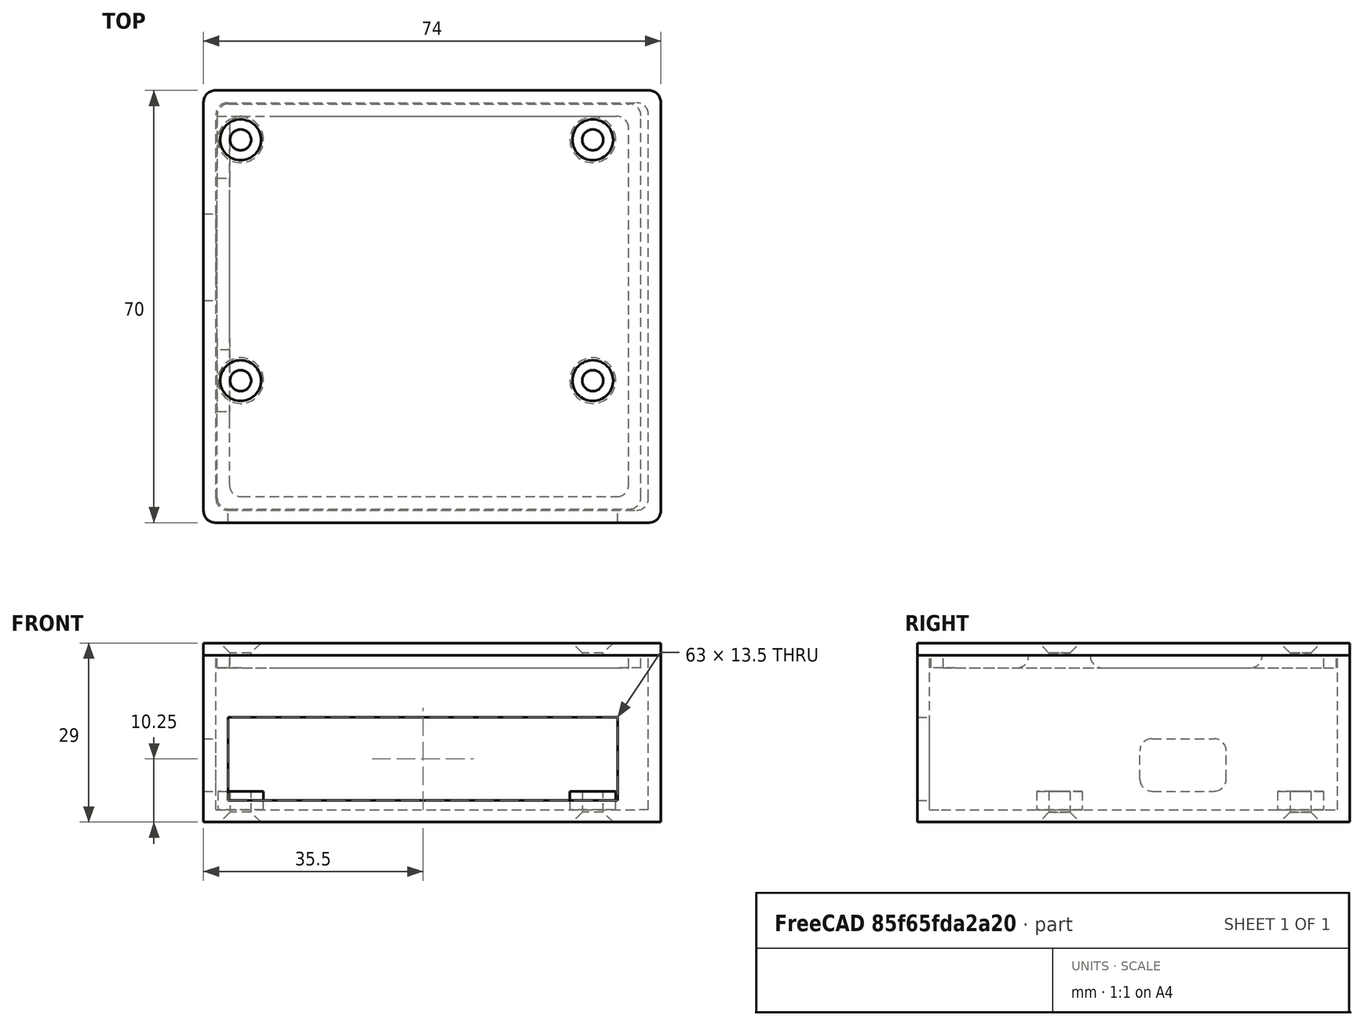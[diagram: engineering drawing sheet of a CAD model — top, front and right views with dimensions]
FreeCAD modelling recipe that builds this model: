
FCSTD DOCUMENT  (FreeCAD 0.20R29410 (Git))
Label: USB_RS232_Adapter_V1
License: All rights reserved
LicenseURL: http://en.wikipedia.org/wiki/All_rights_reserved
objects: Part::Cut×14, Part::Box×9, Part::Cylinder×8, Part::Fillet×6, Part::Fuse×5, Part::Chamfer×2
note: 44 computed .brp shape members not serialized (recipe doc carries the construction recipe); baked Part::Feature solids carry a one-line shape summary decoded from their .brp

FEATURE [Part::Box] Box  label="Würfel"
  AttacherType = Attacher::AttachEngine3D
  Height = 25
  Length = 70
  Placement = pos=(0,-18,0) rot=(0,0,1;0rad)
  Width = 66
FEATURE [Part::Box] Box001  label="Würfel001"
  AttacherType = Attacher::AttachEngine3D
  Height = 27
  Length = 74
  Placement = pos=(-2,-20,-2) rot=(0,0,1;0rad)
  Width = 70
FEATURE [Part::Cut] Cut
  Base = -> Box001
  Tool = -> Box
FEATURE [Part::Cylinder] Cylinder  label="Zylinder"
  Angle = 360
  AttacherType = Attacher::AttachEngine3D
  FirstAngle = 0
  Height = 35
  Placement = pos=(4,3,-2) rot=(0,0,1;0rad)
  Radius = 1.7
  SecondAngle = 0
FEATURE [Part::Cylinder] Cylinder001  label="Zylinder001"
  Angle = 360
  AttacherType = Attacher::AttachEngine3D
  FirstAngle = 0
  Height = 35
  Placement = pos=(61,3,-2) rot=(0,0,1;0rad)
  Radius = 1.7
  SecondAngle = 0
FEATURE [Part::Cylinder] Cylinder002  label="Zylinder002"
  Angle = 360
  AttacherType = Attacher::AttachEngine3D
  FirstAngle = 0
  Height = 33
  Placement = pos=(61,42,-2) rot=(0,0,1;0rad)
  Radius = 1.7
  SecondAngle = 0
FEATURE [Part::Cylinder] Cylinder003  label="Zylinder003"
  Angle = 360
  AttacherType = Attacher::AttachEngine3D
  FirstAngle = 0
  Height = 35
  Placement = pos=(4,42,-2) rot=(0,0,1;0rad)
  Radius = 1.7
  SecondAngle = 0
FEATURE [Part::Box] Box002  label="Würfel002"
  AttacherType = Attacher::AttachEngine3D
  Height = 8.5
  Length = 15
  Placement = pos=(-2,16,3) rot=(0,0,1;0rad)
  Width = 14
FEATURE [Part::Cylinder] Cylinder004  label="Zylinder004"
  Angle = 360
  AttacherType = Attacher::AttachEngine3D
  FirstAngle = 0
  Height = 3
  Placement = pos=(4,3,0) rot=(0,0,1;0rad)
  Radius = 3.7
  SecondAngle = 0
FEATURE [Part::Cylinder] Cylinder005  label="Zylinder005"
  Angle = 360
  AttacherType = Attacher::AttachEngine3D
  FirstAngle = 0
  Height = 3
  Placement = pos=(61,42,0) rot=(0,0,1;0rad)
  Radius = 3.7
  SecondAngle = 0
FEATURE [Part::Cylinder] Cylinder006  label="Zylinder006"
  Angle = 360
  AttacherType = Attacher::AttachEngine3D
  FirstAngle = 0
  Height = 3
  Placement = pos=(61,3,0) rot=(0,0,1;0rad)
  Radius = 3.7
  SecondAngle = 0
FEATURE [Part::Cylinder] Cylinder007  label="Zylinder007"
  Angle = 360
  AttacherType = Attacher::AttachEngine3D
  FirstAngle = 0
  Height = 3
  Placement = pos=(4,42,0) rot=(0,0,1;0rad)
  Radius = 3.7
  SecondAngle = 0
FEATURE [Part::Box] Box003  label="Würfel003"
  AttacherType = Attacher::AttachEngine3D
  Height = 13.5
  Length = 63
  Placement = pos=(2,-28,1.5) rot=(0,0,1;0rad)
  Width = 10
FEATURE [Part::Fuse] Fusion
  Base = -> Cut
  Tool = -> Cylinder004
FEATURE [Part::Fuse] Fusion001
  Base = -> Fusion
  Tool = -> Cylinder005
FEATURE [Part::Fuse] Fusion002
  Base = -> Fusion001
  Tool = -> Cylinder006
FEATURE [Part::Fuse] Fusion003
  Base = -> Fusion002
  Tool = -> Cylinder007
FEATURE [Part::Cut] Cut001
  Base = -> Fusion003
  Tool = -> Cylinder
FEATURE [Part::Cut] Cut002
  Base = -> Cut001
  Tool = -> Cylinder001
FEATURE [Part::Cut] Cut003
  Base = -> Cut002
  Tool = -> Cylinder002
FEATURE [Part::Cut] Cut004
  Base = -> Cut003
  Tool = -> Cylinder003
FEATURE [Part::Cut] Cut005
  Base = -> Cut004
  Tool = -> Box002
FEATURE [Part::Cut] Cut006
  Base = -> Cut005
  Tool = -> Box003
FEATURE [Part::Fillet] Fillet
  Base = -> Cut006
  Edges = 4 edges r=2: [Edge29,Edge31,Edge32,Edge35]
FEATURE [Part::Fillet] Fillet001
  Base = -> Fillet
  Edges = 8 edges r=1.9: [Edge9,Edge11,Edge30,Edge48,Edge49,Edge51,Edge61,Edge62]
FEATURE [Part::Box] Box004  label="Würfel004"
  AttacherType = Attacher::AttachEngine3D
  Height = 2
  Length = 74
  Placement = pos=(-2,-20,25) rot=(0,0,1;0rad)
  Width = 70
FEATURE [Part::Box] Box005  label="Würfel005"
  AttacherType = Attacher::AttachEngine3D
  Height = 2
  Length = 68.6
  Placement = pos=(0.2,-17.8,23) rot=(0,0,1;0rad)
  Width = 65.6
FEATURE [Part::Fillet] Fillet002
  Base = -> Box004
  Edges = 4 edges r=1.9: [Edge1,Edge3,Edge5,Edge7]
FEATURE [Part::Fillet] Fillet003
  Base = -> Box005
  Edges = 4 edges r=1.9: [Edge1,Edge3,Edge5,Edge7]
FEATURE [Part::Box] Box006  label="Würfel006"
  AttacherType = Attacher::AttachEngine3D
  Height = 2
  Length = 64.6
  Placement = pos=(2.2,-15.8,23) rot=(0,0,1;0rad)
  Width = 61.6
FEATURE [Part::Fillet] Fillet004
  Base = -> Box006
  Edges = 4 edges r=1.9: [Edge1,Edge3,Edge5,Edge7]
FEATURE [Part::Cut] Cut007
  Base = -> Fillet003
  Tool = -> Fillet004
FEATURE [Part::Fuse] Fusion004
  Base = -> Fillet002
  Tool = -> Cut007
FEATURE [Part::Cut] Cut008
  Base = -> Fusion004
  Tool = -> Cylinder
FEATURE [Part::Cut] Cut009
  Base = -> Cut008
  Tool = -> Cylinder001
FEATURE [Part::Cut] Cut010
  Base = -> Cut009
  Tool = -> Cylinder002
FEATURE [Part::Cut] Cut011
  Base = -> Cut010
  Tool = -> Cylinder003
FEATURE [Part::Chamfer] Chamfer
  Base = -> Cut011
  Edges = 4 edges r=1.6: [Edge12,Edge13,Edge14,Edge15]
FEATURE [Part::Chamfer] Chamfer001  label="housing"
  Base = -> Fillet001
  Edges = 4 edges r=1.6: [Edge20,Edge21,Edge22,Edge23]
FEATURE [Part::Box] Box007  label="Würfel007"
  AttacherType = Attacher::AttachEngine3D
  Height = 2
  Length = 10
  Placement = pos=(0,-2,22.99) rot=(0,0,1;0rad)
  Width = 10
FEATURE [Part::Box] Box008  label="Würfel008"
  AttacherType = Attacher::AttachEngine3D
  Height = 2
  Length = 10
  Placement = pos=(0,35.8,22.99) rot=(0,0,1;0rad)
  Width = 10
FEATURE [Part::Cut] Cut012
  Base = -> Chamfer
  Tool = -> Box007
FEATURE [Part::Cut] Cut013
  Base = -> Cut012
  Tool = -> Box008
FEATURE [Part::Fillet] Fillet005  label="cap"
  Base = -> Cut013
  Edges = 3 edges r=1.9: [Edge109,Edge115,Edge116]
